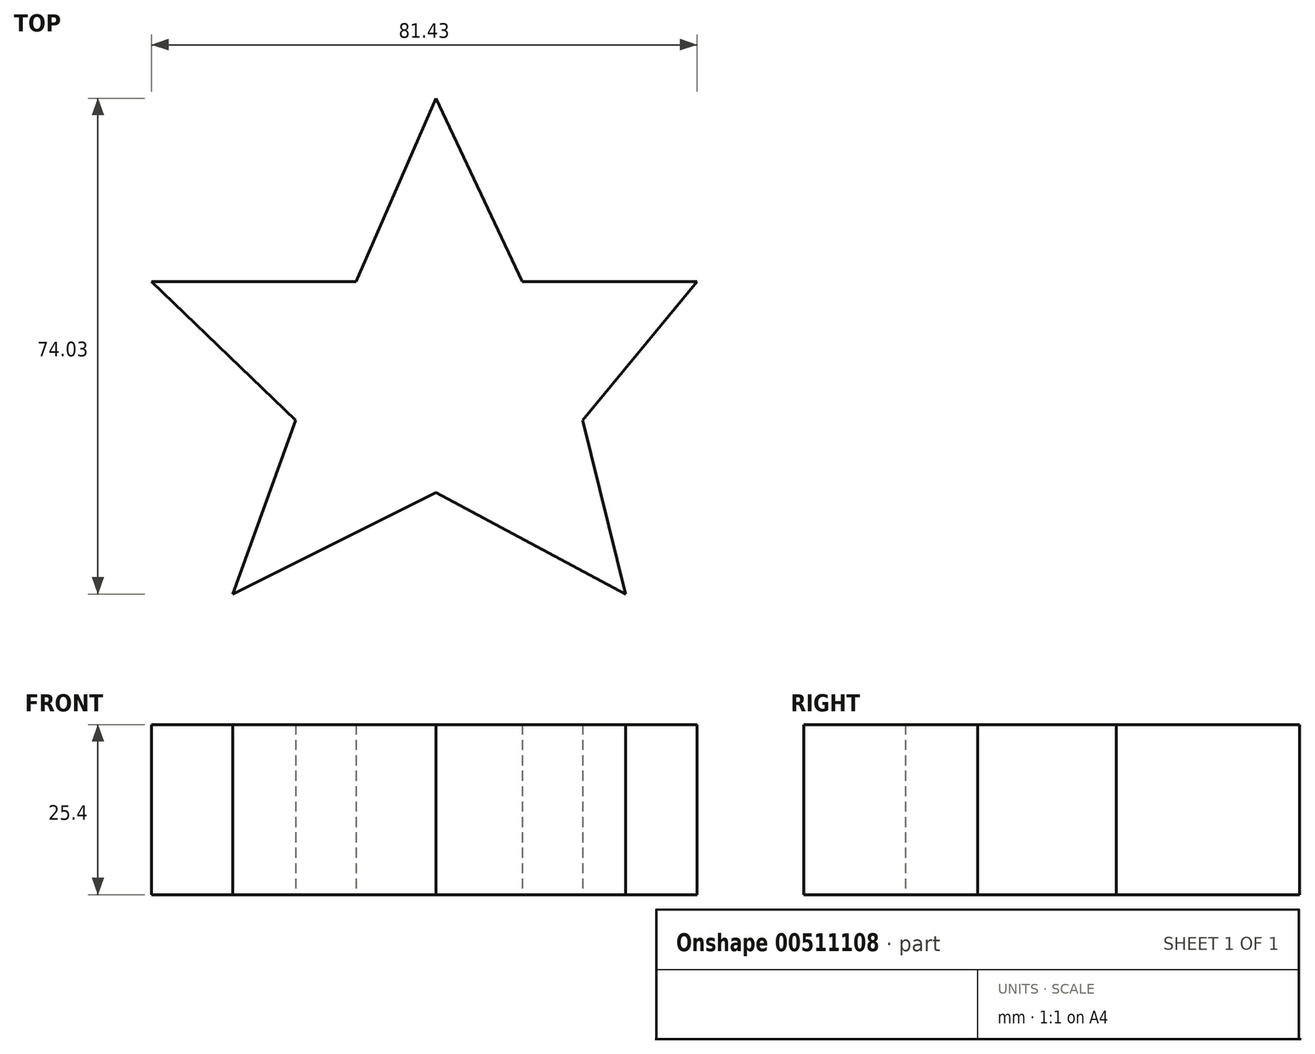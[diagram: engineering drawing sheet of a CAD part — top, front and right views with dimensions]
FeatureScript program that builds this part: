
annotation { "Feature Type Name" : "Feature", "Feature Type Description" : "" }
export const myFeature = defineFeature(function(context is Context, id is Id, definition is map)
    precondition{}
    {
        {
            var Q0;
            Q0=qCreatedBy(makeId("Top.planeOp"),FACE);
            var sketch = newSketch(context, id + "F0", { "sketchPlane" : qUnion([Q0])});
            skLineSegment(sketch, "E0", {"start": v(0, 37.16) * mm, "end": v(-11.95, 9.76) * mm});
            skLineSegment(sketch, "E1", {"start": v(-11.95, 9.76) * mm, "end": v(-42.5, 9.76) * mm});
            skLineSegment(sketch, "E2", {"start": v(-42.5, 9.76) * mm, "end": v(-20.99, -10.93) * mm});
            skLineSegment(sketch, "E3", {"start": v(-20.99, -10.93) * mm, "end": v(-30.39, -36.87) * mm});
            skLineSegment(sketch, "E4", {"start": v(-30.39, -36.87) * mm, "end": v(0, -21.71) * mm});
            skLineSegment(sketch, "E5", {"start": v(0, -21.71) * mm, "end": v(28.27, -36.87) * mm});
            skLineSegment(sketch, "E6", {"start": v(28.27, -36.87) * mm, "end": v(21.86, -10.93) * mm});
            skLineSegment(sketch, "E7", {"start": v(21.86, -10.93) * mm, "end": v(38.93, 9.76) * mm});
            skLineSegment(sketch, "E8", {"start": v(38.93, 9.76) * mm, "end": v(12.87, 9.76) * mm});
            skLineSegment(sketch, "E9", {"start": v(12.87, 9.76) * mm, "end": v(0, 37.16) * mm});
            skSolve(sketch);
        }
        {
            var Q0;
            Q0=makeQuery(id+"F0.imprint","IMPRINT",FACE,{"disambiguationData":[TD([[makeQuery(id+"F0.imprint","IMPRINT",EDGE,{"derivedFrom":sQuery(id+"F0.wireOp",EDGE,"E0")}),1.0]])]});
            var Q1;
            Q1=makeQuery(id+"F0.imprint","IMPRINT",FACE,{"disambiguationData":[TD([[makeQuery(id+"F0.imprint","IMPRINT",EDGE,{"derivedFrom":sQuery(id+"F0.wireOp",EDGE,"E0")}),1.0]])]});
            extrude(context, id + "F1", {"entities" : qUnion([Q0, Q1]), "depth" : 25.4 * mm});
        }
    });
